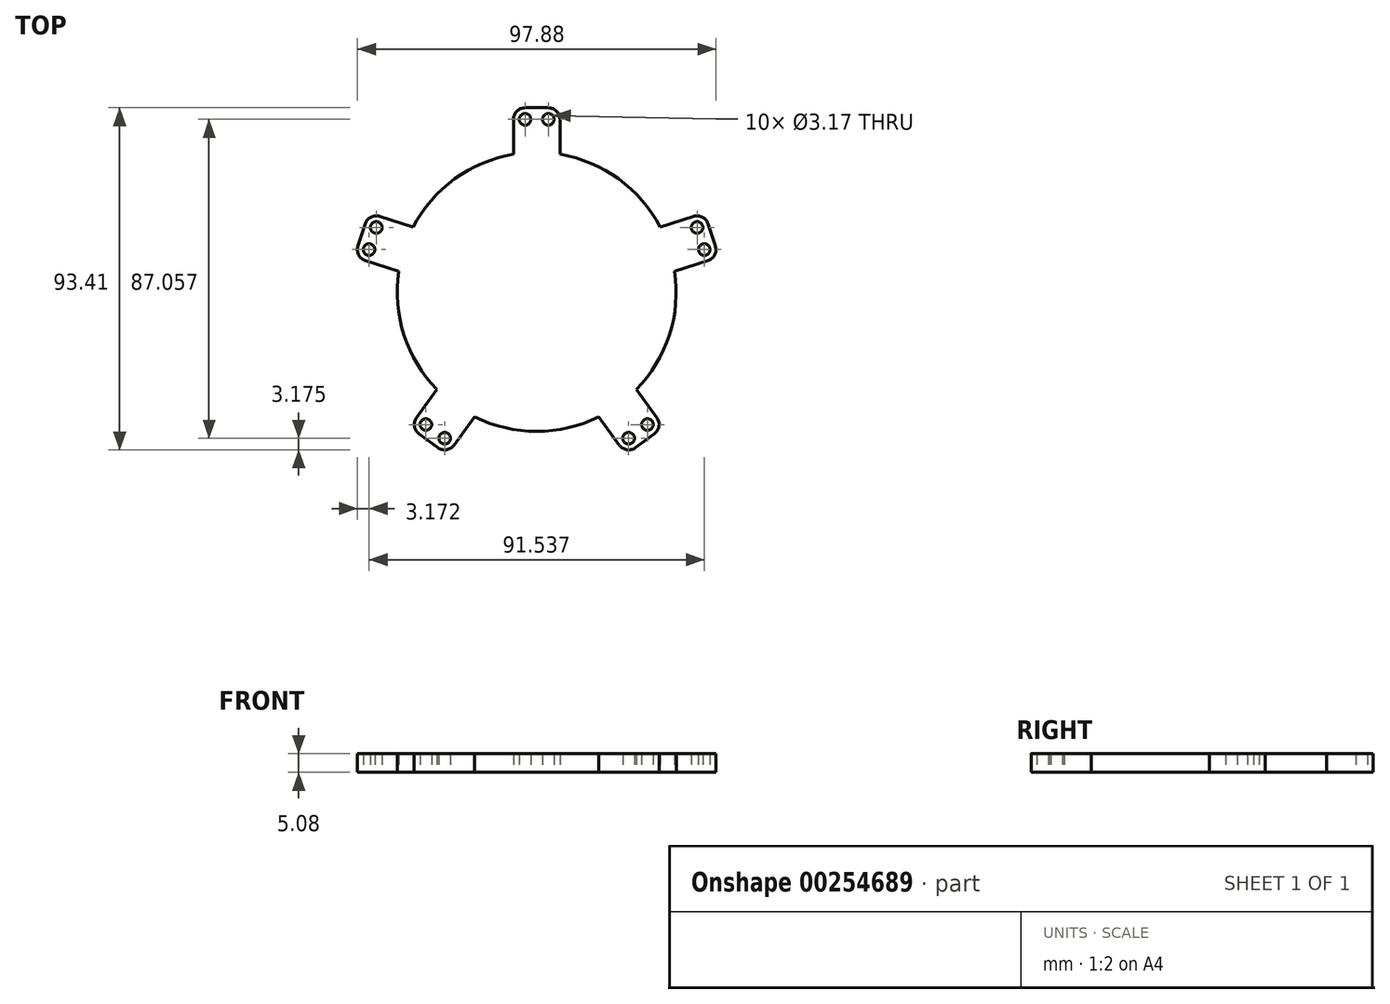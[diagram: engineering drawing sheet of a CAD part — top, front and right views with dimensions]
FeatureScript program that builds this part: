
annotation { "Feature Type Name" : "Feature", "Feature Type Description" : "" }
export const myFeature = defineFeature(function(context is Context, id is Id, definition is map)
    precondition{}
    {
        {
            var Q0;
            Q0=qCreatedBy(makeId("Top.planeOp"),FACE);
            var sketch = newSketch(context, id + "F0", { "sketchPlane" : qUnion([Q0])});
            skCircle(sketch, "E0", {"center": v(0, 0) * mm, "radius": 38.1 * mm});
            skLineSegment(sketch, "E1", {"start": v(0, 0) * mm, "end": v(0, 50.8) * mm, "construction": true});
            skLineSegment(sketch, "E2", {"start": v(-6.35, 37.57) * mm, "end": v(-6.35, 47.1) * mm});
            skLineSegment(sketch, "E3.MirrorCS", {"start": v(6.35, 37.57) * mm, "end": v(6.35, 47.1) * mm});
            skLineSegment(sketch, "E4", {"start": v(-3.18, 50.27) * mm, "end": v(3.17, 50.27) * mm});
            skCircle(sketch, "E5", {"center": v(-3.17, 47.1) * mm, "radius": 1.59 * mm});
            skCircle(sketch, "E6.MirrorC", {"center": v(3.17, 47.1) * mm, "radius": 1.59 * mm});
            skArc(sketch, "E7.filletArc", {"start": v(6.35, 47.1) * mm, "mid": v(5.42, 49.34) * mm, "end": v(3.17, 50.27) * mm});
            skArc(sketch, "E8.filletArc", {"start": v(-3.18, 50.27) * mm, "mid": v(-5.42, 49.34) * mm, "end": v(-6.35, 47.1) * mm});
            skArc(sketch, "E9.1.0", {"start": v(-48.79, 12.51) * mm, "mid": v(-48.6, 10.1) * mm, "end": v(-46.75, 8.51) * mm});
            skLineSegment(sketch, "E9.1.1", {"start": v(-33.77, 17.65) * mm, "end": v(-42.82, 20.6) * mm});
            skLineSegment(sketch, "E9.1.2", {"start": v(-37.7, 5.57) * mm, "end": v(-46.75, 8.51) * mm});
            skCircle(sketch, "E9.1.3", {"center": v(-45.77, 11.53) * mm, "radius": 1.59 * mm});
            skLineSegment(sketch, "E9.1.4", {"start": v(-48.79, 12.51) * mm, "end": v(-46.83, 18.55) * mm});
            skCircle(sketch, "E9.1.5", {"center": v(-43.8, 17.57) * mm, "radius": 1.59 * mm});
            skArc(sketch, "E9.1.6", {"start": v(-42.82, 20.6) * mm, "mid": v(-45.25, 20.4) * mm, "end": v(-46.83, 18.55) * mm});
            skArc(sketch, "E9.2.0", {"start": v(-26.98, -42.53) * mm, "mid": v(-24.61, -43.1) * mm, "end": v(-22.54, -41.83) * mm});
            skLineSegment(sketch, "E9.2.1", {"start": v(-27.22, -26.66) * mm, "end": v(-32.82, -34.37) * mm});
            skLineSegment(sketch, "E9.2.2", {"start": v(-16.94, -34.12) * mm, "end": v(-22.54, -41.83) * mm});
            skCircle(sketch, "E9.2.3", {"center": v(-25.11, -39.96) * mm, "radius": 1.59 * mm});
            skLineSegment(sketch, "E9.2.4", {"start": v(-26.98, -42.53) * mm, "end": v(-32.11, -38.8) * mm});
            skCircle(sketch, "E9.2.5", {"center": v(-30.25, -36.23) * mm, "radius": 1.59 * mm});
            skArc(sketch, "E9.2.6", {"start": v(-32.82, -34.37) * mm, "mid": v(-33.38, -36.73) * mm, "end": v(-32.11, -38.8) * mm});
            skArc(sketch, "E9.3.0", {"start": v(32.11, -38.8) * mm, "mid": v(33.38, -36.73) * mm, "end": v(32.82, -34.37) * mm});
            skLineSegment(sketch, "E9.3.1", {"start": v(16.94, -34.12) * mm, "end": v(22.54, -41.83) * mm});
            skLineSegment(sketch, "E9.3.2", {"start": v(27.22, -26.66) * mm, "end": v(32.82, -34.37) * mm});
            skCircle(sketch, "E9.3.3", {"center": v(30.25, -36.23) * mm, "radius": 1.59 * mm});
            skLineSegment(sketch, "E9.3.4", {"start": v(32.11, -38.8) * mm, "end": v(26.98, -42.53) * mm});
            skCircle(sketch, "E9.3.5", {"center": v(25.11, -39.96) * mm, "radius": 1.59 * mm});
            skArc(sketch, "E9.3.6", {"start": v(22.54, -41.83) * mm, "mid": v(24.61, -43.1) * mm, "end": v(26.98, -42.53) * mm});
            skArc(sketch, "E9.4.0", {"start": v(46.83, 18.55) * mm, "mid": v(45.25, 20.4) * mm, "end": v(42.82, 20.6) * mm});
            skLineSegment(sketch, "E9.4.1", {"start": v(37.7, 5.57) * mm, "end": v(46.75, 8.51) * mm});
            skLineSegment(sketch, "E9.4.2", {"start": v(33.77, 17.65) * mm, "end": v(42.82, 20.6) * mm});
            skCircle(sketch, "E9.4.3", {"center": v(43.8, 17.57) * mm, "radius": 1.59 * mm});
            skLineSegment(sketch, "E9.4.4", {"start": v(46.83, 18.55) * mm, "end": v(48.79, 12.51) * mm});
            skCircle(sketch, "E9.4.5", {"center": v(45.77, 11.53) * mm, "radius": 1.59 * mm});
            skArc(sketch, "E9.4.6", {"start": v(46.75, 8.51) * mm, "mid": v(48.6, 10.1) * mm, "end": v(48.79, 12.51) * mm});
            skSolve(sketch);
        }
        {
            var Q0;
            Q0 = qSketchRegion(id + "F0", true);
            extrude(context, id + "F1", {"entities" : qUnion([Q0]), "depth" : 5.08 * mm});
        }
    });
